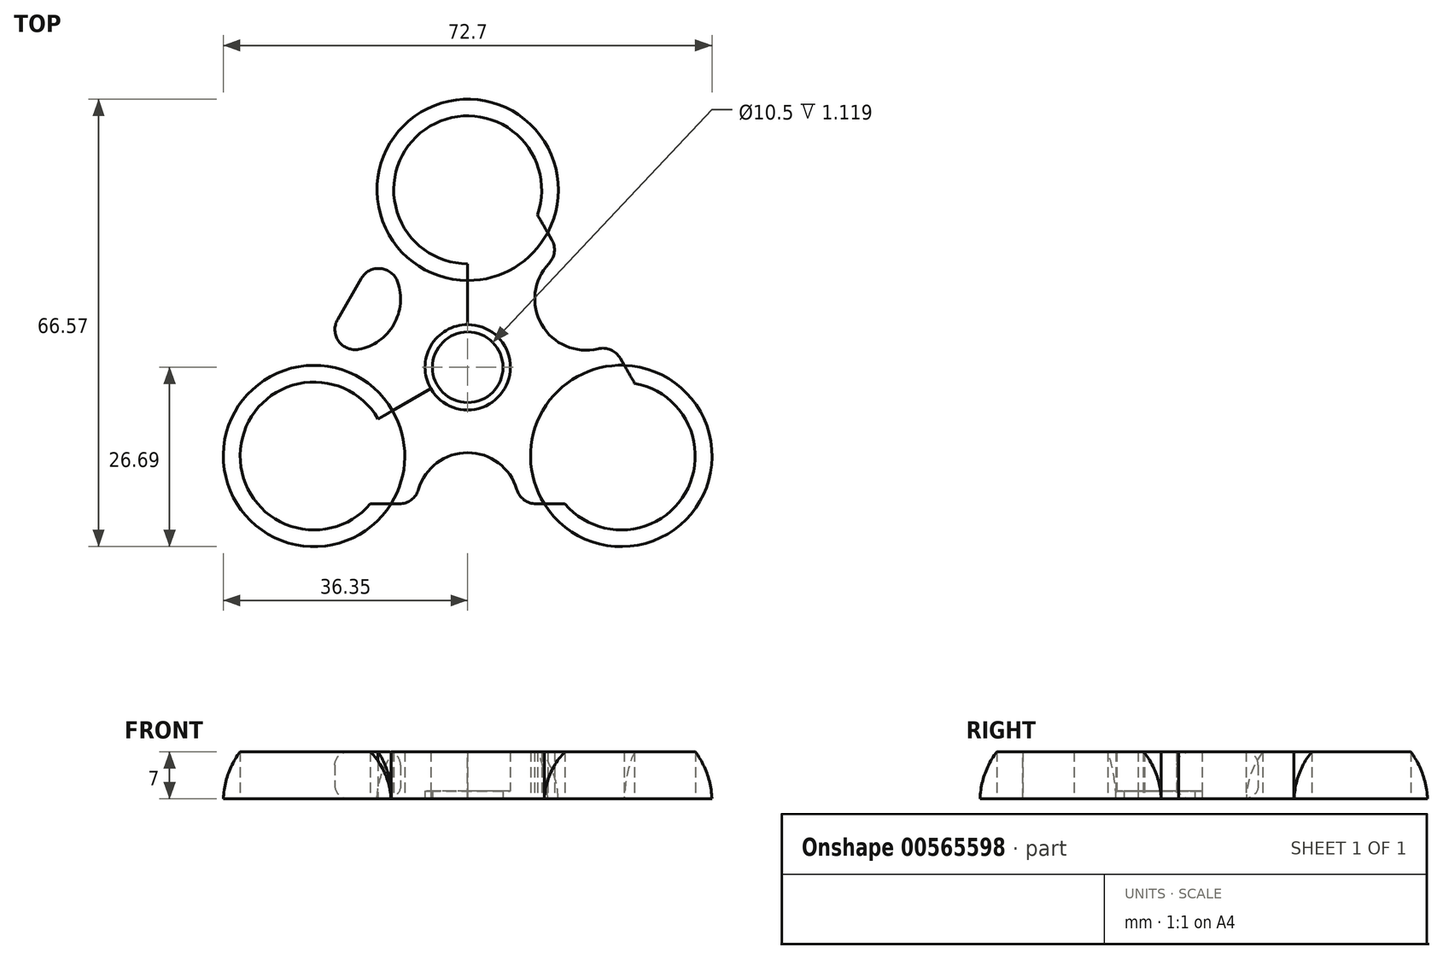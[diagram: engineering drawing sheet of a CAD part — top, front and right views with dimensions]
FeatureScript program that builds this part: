
annotation { "Feature Type Name" : "Feature", "Feature Type Description" : "" }
export const myFeature = defineFeature(function(context is Context, id is Id, definition is map)
    precondition{}
    {
        {
            var Q0;
            Q0=qCreatedBy(makeId("Top.planeOp"),FACE);
            var sketch = newSketch(context, id + "F0", { "sketchPlane" : qUnion([Q0])});
            skCircle(sketch, "E0", {"center": v(0, 0) * mm, "radius": 6.35 * mm});
            skLineSegment(sketch, "E1", {"start": v(0, 0) * mm, "end": v(0, 26.4) * mm});
            skLineSegment(sketch, "E2", {"start": v(0, 0) * mm, "end": v(22.86, -13.2) * mm});
            skLineSegment(sketch, "E3", {"start": v(0, 0) * mm, "end": v(-22.86, -13.2) * mm});
            skCircle(sketch, "E4", {"center": v(-22.86, -13.2) * mm, "radius": 11 * mm});
            skCircle(sketch, "E5", {"center": v(22.86, -13.2) * mm, "radius": 11 * mm});
            skCircle(sketch, "E6", {"center": v(0, 26.4) * mm, "radius": 11 * mm});
            skLineSegment(sketch, "E7", {"start": v(0, 0) * mm, "end": v(-35.2, -20.32) * mm});
            skLineSegment(sketch, "E8", {"start": v(0, 0) * mm, "end": v(35.2, -20.32) * mm});
            skLineSegment(sketch, "E9", {"start": v(0, 0) * mm, "end": v(0, 40.64) * mm});
            skLineSegment(sketch, "E10", {"start": v(-35.2, -20.32) * mm, "end": v(35.2, -20.32) * mm});
            skLineSegment(sketch, "E11", {"start": v(0, 40.64) * mm, "end": v(35.2, -20.32) * mm});
            skLineSegment(sketch, "E12", {"start": v(0, 40.64) * mm, "end": v(-35.2, -20.32) * mm});
            skCircle(sketch, "E13", {"center": v(-22.86, -13.2) * mm, "radius": 13.5 * mm});
            skCircle(sketch, "E14", {"center": v(22.86, -13.2) * mm, "radius": 13.5 * mm});
            skCircle(sketch, "E15", {"center": v(0, 26.4) * mm, "radius": 13.5 * mm});
            skArc(sketch, "E16", {"start": v(-13.79, 16.76) * mm, "mid": v(-11, 6.35) * mm, "end": v(-21.4, 3.56) * mm});
            skArc(sketch, "E17", {"start": v(13.79, 16.76) * mm, "mid": v(11, 6.35) * mm, "end": v(21.4, 3.56) * mm});
            skArc(sketch, "E18", {"start": v(7.62, -20.32) * mm, "mid": v(0, -12.7) * mm, "end": v(-7.62, -20.32) * mm});
            skCircle(sketch, "E19", {"center": v(0, 0) * mm, "radius": 5.25 * mm});
            skSolve(sketch);
        }
        {
            var Q0;
            {var subQ0=sQuery(id+"F0.wireOp",EDGE,"E10");var subQ1=sQuery(id+"F0.wireOp",EDGE,"E5");var subQ2=makeQuery(id+"F0.imprint","INTERSECT",VERTEX,{"disambiguationData":[OD(0.0)],"derivedFrom":[subQ1,subQ0]});Q0=makeQuery(id+"F0.imprint","IMPRINT",FACE,{"disambiguationData":[TD([[makeQuery(id+"F0.imprint","IMPRINT",EDGE,{"disambiguationData":[TD([[subQ2,-1.0]])],"derivedFrom":subQ1}),-1.0]])]});}
            var Q1;
            {var subQ0=sQuery(id+"F0.wireOp",EDGE,"E8");var subQ1=sQuery(id+"F0.wireOp",EDGE,"E5");var subQ2=makeQuery(id+"F0.imprint","INTERSECT",VERTEX,{"disambiguationData":[OD(1.0)],"derivedFrom":[subQ1,subQ0]});Q1=makeQuery(id+"F0.imprint","IMPRINT",FACE,{"disambiguationData":[TD([[makeQuery(id+"F0.imprint","IMPRINT",EDGE,{"disambiguationData":[TD([[subQ2,-1.0]])],"derivedFrom":subQ1}),-1.0]])]});}
            var Q2;
            {var subQ0=sQuery(id+"F0.wireOp",EDGE,"E10");var subQ1=sQuery(id+"F0.wireOp",EDGE,"E5");var subQ2=makeQuery(id+"F0.imprint","INTERSECT",VERTEX,{"disambiguationData":[OD(1.0)],"derivedFrom":[subQ1,subQ0]});Q2=makeQuery(id+"F0.imprint","IMPRINT",FACE,{"disambiguationData":[TD([[makeQuery(id+"F0.imprint","IMPRINT",EDGE,{"disambiguationData":[TD([[subQ2,-1.0]])],"derivedFrom":subQ1}),-1.0]])]});}
            var Q3;
            {var subQ0=sQuery(id+"F0.wireOp",EDGE,"E11");var subQ1=sQuery(id+"F0.wireOp",EDGE,"E5");var subQ2=makeQuery(id+"F0.imprint","INTERSECT",VERTEX,{"disambiguationData":[OD(0.0)],"derivedFrom":[subQ1,subQ0]});Q3=makeQuery(id+"F0.imprint","IMPRINT",FACE,{"disambiguationData":[TD([[makeQuery(id+"F0.imprint","IMPRINT",EDGE,{"disambiguationData":[TD([[subQ2,1.0]])],"derivedFrom":subQ1}),-1.0]])]});}
            var Q4;
            {var subQ0=sQuery(id+"F0.wireOp",EDGE,"E8");var subQ1=sQuery(id+"F0.wireOp",EDGE,"E5");var subQ2=makeQuery(id+"F0.imprint","INTERSECT",VERTEX,{"disambiguationData":[OD(0.0)],"derivedFrom":[subQ1,subQ0]});Q4=makeQuery(id+"F0.imprint","IMPRINT",FACE,{"disambiguationData":[TD([[makeQuery(id+"F0.imprint","IMPRINT",EDGE,{"disambiguationData":[TD([[subQ2,1.0]])],"derivedFrom":subQ1}),-1.0]])]});}
            var Q5;
            {var subQ0=sQuery(id+"F0.wireOp",EDGE,"E8");var subQ1=sQuery(id+"F0.wireOp",EDGE,"E5");var subQ2=makeQuery(id+"F0.imprint","INTERSECT",VERTEX,{"disambiguationData":[OD(0.0)],"derivedFrom":[subQ1,subQ0]});Q5=makeQuery(id+"F0.imprint","IMPRINT",FACE,{"disambiguationData":[TD([[makeQuery(id+"F0.imprint","IMPRINT",EDGE,{"disambiguationData":[TD([[subQ2,-1.0]])],"derivedFrom":subQ1}),-1.0]])]});}
            var Q6;
            {var subQ5=sQuery(id+"F0.wireOp",EDGE,"E18");Q6=makeQuery(id+"F0.imprint","IMPRINT",FACE,{"disambiguationData":[TD([[makeQuery(id+"F0.imprint","IMPRINT",EDGE,{"derivedFrom":subQ5}),-1.0]])]});}
            var Q7;
            {var subQ11=sQuery(id+"F0.wireOp",EDGE,"E17");Q7=makeQuery(id+"F0.imprint","IMPRINT",FACE,{"disambiguationData":[TD([[makeQuery(id+"F0.imprint","IMPRINT",EDGE,{"derivedFrom":subQ11}),-1.0]])]});}
            var Q8;
            {var subQ0=sQuery(id+"F0.wireOp",EDGE,"E16");Q8=makeQuery(id+"F0.imprint","IMPRINT",FACE,{"disambiguationData":[TD([[makeQuery(id+"F0.imprint","IMPRINT",EDGE,{"derivedFrom":subQ0}),1.0]])]});}
            var Q9;
            {var subQ0=sQuery(id+"F0.wireOp",EDGE,"E12");var subQ1=sQuery(id+"F0.wireOp",EDGE,"E4");var subQ2=makeQuery(id+"F0.imprint","INTERSECT",VERTEX,{"disambiguationData":[OD(0.0)],"derivedFrom":[subQ1,subQ0]});Q9=makeQuery(id+"F0.imprint","IMPRINT",FACE,{"disambiguationData":[TD([[makeQuery(id+"F0.imprint","IMPRINT",EDGE,{"disambiguationData":[TD([[subQ2,1.0]])],"derivedFrom":subQ1}),-1.0]])]});}
            var Q10;
            {var subQ0=sQuery(id+"F0.wireOp",EDGE,"E7");var subQ1=sQuery(id+"F0.wireOp",EDGE,"E4");var subQ2=makeQuery(id+"F0.imprint","INTERSECT",VERTEX,{"disambiguationData":[OD(0.0)],"derivedFrom":[subQ1,subQ0]});Q10=makeQuery(id+"F0.imprint","IMPRINT",FACE,{"disambiguationData":[TD([[makeQuery(id+"F0.imprint","IMPRINT",EDGE,{"disambiguationData":[TD([[subQ2,1.0]])],"derivedFrom":subQ1}),-1.0]])]});}
            var Q11;
            {var subQ0=sQuery(id+"F0.wireOp",EDGE,"E10");var subQ1=sQuery(id+"F0.wireOp",EDGE,"E4");var subQ2=makeQuery(id+"F0.imprint","INTERSECT",VERTEX,{"disambiguationData":[OD(0.0)],"derivedFrom":[subQ1,subQ0]});Q11=makeQuery(id+"F0.imprint","IMPRINT",FACE,{"disambiguationData":[TD([[makeQuery(id+"F0.imprint","IMPRINT",EDGE,{"disambiguationData":[TD([[subQ2,-1.0]])],"derivedFrom":subQ1}),-1.0]])]});}
            var Q12;
            {var subQ0=sQuery(id+"F0.wireOp",EDGE,"E12");var subQ1=sQuery(id+"F0.wireOp",EDGE,"E4");var subQ2=makeQuery(id+"F0.imprint","INTERSECT",VERTEX,{"disambiguationData":[OD(1.0)],"derivedFrom":[subQ1,subQ0]});Q12=makeQuery(id+"F0.imprint","IMPRINT",FACE,{"disambiguationData":[TD([[makeQuery(id+"F0.imprint","IMPRINT",EDGE,{"disambiguationData":[TD([[subQ2,-1.0]])],"derivedFrom":subQ1}),-1.0]])]});}
            var Q13;
            {var subQ0=sQuery(id+"F0.wireOp",EDGE,"E7");var subQ1=sQuery(id+"F0.wireOp",EDGE,"E4");var subQ2=makeQuery(id+"F0.imprint","INTERSECT",VERTEX,{"disambiguationData":[OD(1.0)],"derivedFrom":[subQ1,subQ0]});Q13=makeQuery(id+"F0.imprint","IMPRINT",FACE,{"disambiguationData":[TD([[makeQuery(id+"F0.imprint","IMPRINT",EDGE,{"disambiguationData":[TD([[subQ2,-1.0]])],"derivedFrom":subQ1}),-1.0]])]});}
            var Q14;
            {var subQ0=sQuery(id+"F0.wireOp",EDGE,"E12");var subQ1=sQuery(id+"F0.wireOp",EDGE,"E4");var subQ2=makeQuery(id+"F0.imprint","INTERSECT",VERTEX,{"disambiguationData":[OD(0.0)],"derivedFrom":[subQ1,subQ0]});Q14=makeQuery(id+"F0.imprint","IMPRINT",FACE,{"disambiguationData":[TD([[makeQuery(id+"F0.imprint","IMPRINT",EDGE,{"disambiguationData":[TD([[subQ2,-1.0]])],"derivedFrom":subQ1}),-1.0]])]});}
            var Q15;
            {var subQ0=sQuery(id+"F0.wireOp",EDGE,"E9");var subQ1=sQuery(id+"F0.wireOp",EDGE,"E6");var subQ2=makeQuery(id+"F0.imprint","INTERSECT",VERTEX,{"disambiguationData":[OD(1.0)],"derivedFrom":[subQ1,subQ0]});Q15=makeQuery(id+"F0.imprint","IMPRINT",FACE,{"disambiguationData":[TD([[makeQuery(id+"F0.imprint","IMPRINT",EDGE,{"disambiguationData":[TD([[subQ2,-1.0]])],"derivedFrom":subQ1}),-1.0]])]});}
            var Q16;
            {var subQ0=sQuery(id+"F0.wireOp",EDGE,"E12");var subQ1=sQuery(id+"F0.wireOp",EDGE,"E6");var subQ2=makeQuery(id+"F0.imprint","INTERSECT",VERTEX,{"disambiguationData":[OD(1.0)],"derivedFrom":[subQ1,subQ0]});Q16=makeQuery(id+"F0.imprint","IMPRINT",FACE,{"disambiguationData":[TD([[makeQuery(id+"F0.imprint","IMPRINT",EDGE,{"disambiguationData":[TD([[subQ2,-1.0]])],"derivedFrom":subQ1}),-1.0]])]});}
            var Q17;
            {var subQ0=sQuery(id+"F0.wireOp",EDGE,"E12");var subQ1=sQuery(id+"F0.wireOp",EDGE,"E6");var subQ2=makeQuery(id+"F0.imprint","INTERSECT",VERTEX,{"disambiguationData":[OD(0.0)],"derivedFrom":[subQ1,subQ0]});Q17=makeQuery(id+"F0.imprint","IMPRINT",FACE,{"disambiguationData":[TD([[makeQuery(id+"F0.imprint","IMPRINT",EDGE,{"disambiguationData":[TD([[subQ2,-1.0]])],"derivedFrom":subQ1}),-1.0]])]});}
            var Q18;
            {var subQ0=sQuery(id+"F0.wireOp",EDGE,"E11");var subQ1=sQuery(id+"F0.wireOp",EDGE,"E6");var subQ2=makeQuery(id+"F0.imprint","INTERSECT",VERTEX,{"disambiguationData":[OD(0.0)],"derivedFrom":[subQ1,subQ0]});Q18=makeQuery(id+"F0.imprint","IMPRINT",FACE,{"disambiguationData":[TD([[makeQuery(id+"F0.imprint","IMPRINT",EDGE,{"disambiguationData":[TD([[subQ2,1.0]])],"derivedFrom":subQ1}),-1.0]])]});}
            var Q19;
            {var subQ0=sQuery(id+"F0.wireOp",EDGE,"E9");var subQ1=sQuery(id+"F0.wireOp",EDGE,"E6");var subQ2=makeQuery(id+"F0.imprint","INTERSECT",VERTEX,{"disambiguationData":[OD(0.0)],"derivedFrom":[subQ1,subQ0]});Q19=makeQuery(id+"F0.imprint","IMPRINT",FACE,{"disambiguationData":[TD([[makeQuery(id+"F0.imprint","IMPRINT",EDGE,{"disambiguationData":[TD([[subQ2,1.0]])],"derivedFrom":subQ1}),-1.0]])]});}
            var Q20;
            {var subQ0=sQuery(id+"F0.wireOp",EDGE,"E9");var subQ1=sQuery(id+"F0.wireOp",EDGE,"E6");var subQ2=makeQuery(id+"F0.imprint","INTERSECT",VERTEX,{"disambiguationData":[OD(0.0)],"derivedFrom":[subQ1,subQ0]});Q20=makeQuery(id+"F0.imprint","IMPRINT",FACE,{"disambiguationData":[TD([[makeQuery(id+"F0.imprint","IMPRINT",EDGE,{"disambiguationData":[TD([[subQ2,-1.0]])],"derivedFrom":subQ1}),-1.0]])]});}
            extrude(context, id + "F1", {"entities" : qUnion([Q0, Q1, Q2, Q3, Q4, Q5, Q6, Q7, Q8, Q9, Q10, Q11, Q12, Q13, Q14, Q15, Q16, Q17, Q18, Q19, Q20]), "depth" : 7 * mm, "offsetDistance" : 25.4 * mm});
        }
        {
            var Q0;
            {var subQ0=sQuery(id+"F0.wireOp",EDGE,"E18");var subQ1=sQuery(id+"F0.wireOp",EDGE,"E10");Q0=makeQuery(id+"F1.opExtrude","SWEPT_EDGE",EDGE,{"disambiguationData":[OSD([subQ1,subQ0]),TDD([makeQuery(id+"F0.imprint","INTERSECT",VERTEX,{"disambiguationData":[OD(1.0)],"derivedFrom":[subQ1,subQ0]})])]});}
            var Q1;
            {var subQ0=sQuery(id+"F0.wireOp",EDGE,"E18");var subQ1=sQuery(id+"F0.wireOp",EDGE,"E10");Q1=makeQuery(id+"F1.opExtrude","SWEPT_EDGE",EDGE,{"disambiguationData":[OSD([subQ1,subQ0]),TDD([makeQuery(id+"F0.imprint","INTERSECT",VERTEX,{"disambiguationData":[OD(0.0)],"derivedFrom":[subQ1,subQ0]})])]});}
            var Q2;
            {var subQ0=sQuery(id+"F0.wireOp",EDGE,"E16");var subQ1=sQuery(id+"F0.wireOp",EDGE,"E12");Q2=makeQuery(id+"F1.opExtrude","SWEPT_EDGE",EDGE,{"disambiguationData":[OSD([subQ1,subQ0]),TDD([makeQuery(id+"F0.imprint","INTERSECT",VERTEX,{"disambiguationData":[OD(0.0)],"derivedFrom":[subQ1,subQ0]})])]});}
            var Q3;
            {var subQ0=sQuery(id+"F0.wireOp",EDGE,"E16");var subQ1=sQuery(id+"F0.wireOp",EDGE,"E12");Q3=makeQuery(id+"F1.opExtrude","SWEPT_EDGE",EDGE,{"disambiguationData":[OSD([subQ1,subQ0]),TDD([makeQuery(id+"F0.imprint","INTERSECT",VERTEX,{"disambiguationData":[OD(1.0)],"derivedFrom":[subQ1,subQ0]})])]});}
            var Q4;
            {var subQ0=sQuery(id+"F0.wireOp",EDGE,"E17");var subQ1=sQuery(id+"F0.wireOp",EDGE,"E11");Q4=makeQuery(id+"F1.opExtrude","SWEPT_EDGE",EDGE,{"disambiguationData":[OSD([subQ1,subQ0]),TDD([makeQuery(id+"F0.imprint","INTERSECT",VERTEX,{"disambiguationData":[OD(1.0)],"derivedFrom":[subQ1,subQ0]})])]});}
            var Q5;
            {var subQ0=sQuery(id+"F0.wireOp",EDGE,"E17");var subQ1=sQuery(id+"F0.wireOp",EDGE,"E11");Q5=makeQuery(id+"F1.opExtrude","SWEPT_EDGE",EDGE,{"disambiguationData":[OSD([subQ1,subQ0]),TDD([makeQuery(id+"F0.imprint","INTERSECT",VERTEX,{"disambiguationData":[OD(0.0)],"derivedFrom":[subQ1,subQ0]})])]});}
            fillet(context, id + "F2", {"entities" : qUnion([Q0, Q1, Q2, Q3, Q4, Q5]), "radius" : 3 * mm, "tangentPropagation" : true, "allowEdgeOverflow" : false});
        }
        {
            var Q0;
            Q0=makeQuery(id+"F1.opExtrude","CAP_EDGE",EDGE,{"disambiguationData":[OSD([sQuery(id+"F0.wireOp",EDGE,"E15")])],"isStart":false});
            var Q1;
            {var subQ0=sQuery(id+"F0.wireOp",EDGE,"E11");Q1=makeQuery(id+"F1.opExtrude","CAP_EDGE",EDGE,{"disambiguationData":[OSD([subQ0]),TDD([makeQuery(id+"F0.imprint","IMPRINT",EDGE,{"disambiguationData":[TD([[makeQuery(id+"F0.imprint","INTERSECT",VERTEX,{"disambiguationData":[OD(0.0)],"derivedFrom":[subQ0,sQuery(id+"F0.wireOp",EDGE,"E17")]}),1.0]])],"derivedFrom":subQ0})])],"isStart":false});}
            var Q2;
            {var subQ0=sQuery(id+"F0.wireOp",EDGE,"E17");var subQ1=sQuery(id+"F0.wireOp",EDGE,"E11");Q2=makeQuery(id+"F2.opFillet","BLEND_EDGE",EDGE,{"blendedFrom":[makeQuery(id+"F1.opExtrude","SWEPT_EDGE",EDGE,{"disambiguationData":[OSD([subQ1,subQ0]),TDD([makeQuery(id+"F0.imprint","INTERSECT",VERTEX,{"disambiguationData":[OD(0.0)],"derivedFrom":[subQ1,subQ0]})])]}),makeQuery(id+"F1.opExtrude","CAP_FACE",FACE,{"disambiguationData":[OSD([sQuery(id+"F0.wireOp",EDGE,"E0"),sQuery(id+"F0.wireOp",EDGE,"E4"),sQuery(id+"F0.wireOp",EDGE,"E5"),sQuery(id+"F0.wireOp",EDGE,"E6"),sQuery(id+"F0.wireOp",EDGE,"E10"),subQ1,sQuery(id+"F0.wireOp",EDGE,"E12"),sQuery(id+"F0.wireOp",EDGE,"E13"),sQuery(id+"F0.wireOp",EDGE,"E14"),sQuery(id+"F0.wireOp",EDGE,"E15"),sQuery(id+"F0.wireOp",EDGE,"E16"),subQ0,sQuery(id+"F0.wireOp",EDGE,"E18")])],"isStart":false})],"blendedInto":[makeQuery(id+"F1.opExtrude","CAP_FACE",FACE,{"disambiguationData":[OSD([sQuery(id+"F0.wireOp",EDGE,"E0"),sQuery(id+"F0.wireOp",EDGE,"E4"),sQuery(id+"F0.wireOp",EDGE,"E5"),sQuery(id+"F0.wireOp",EDGE,"E6"),sQuery(id+"F0.wireOp",EDGE,"E10"),subQ1,sQuery(id+"F0.wireOp",EDGE,"E12"),sQuery(id+"F0.wireOp",EDGE,"E13"),sQuery(id+"F0.wireOp",EDGE,"E14"),sQuery(id+"F0.wireOp",EDGE,"E15"),sQuery(id+"F0.wireOp",EDGE,"E16"),subQ0,sQuery(id+"F0.wireOp",EDGE,"E18")])],"isStart":false})]});}
            var Q3;
            Q3=makeQuery(id+"F1.opExtrude","CAP_EDGE",EDGE,{"disambiguationData":[OSD([sQuery(id+"F0.wireOp",EDGE,"E17")])],"isStart":false});
            var Q4;
            {var subQ0=sQuery(id+"F0.wireOp",EDGE,"E17");var subQ1=sQuery(id+"F0.wireOp",EDGE,"E11");Q4=makeQuery(id+"F2.opFillet","BLEND_EDGE",EDGE,{"blendedFrom":[makeQuery(id+"F1.opExtrude","SWEPT_EDGE",EDGE,{"disambiguationData":[OSD([subQ1,subQ0]),TDD([makeQuery(id+"F0.imprint","INTERSECT",VERTEX,{"disambiguationData":[OD(1.0)],"derivedFrom":[subQ1,subQ0]})])]}),makeQuery(id+"F1.opExtrude","CAP_FACE",FACE,{"disambiguationData":[OSD([sQuery(id+"F0.wireOp",EDGE,"E0"),sQuery(id+"F0.wireOp",EDGE,"E4"),sQuery(id+"F0.wireOp",EDGE,"E5"),sQuery(id+"F0.wireOp",EDGE,"E6"),sQuery(id+"F0.wireOp",EDGE,"E10"),subQ1,sQuery(id+"F0.wireOp",EDGE,"E12"),sQuery(id+"F0.wireOp",EDGE,"E13"),sQuery(id+"F0.wireOp",EDGE,"E14"),sQuery(id+"F0.wireOp",EDGE,"E15"),sQuery(id+"F0.wireOp",EDGE,"E16"),subQ0,sQuery(id+"F0.wireOp",EDGE,"E18")])],"isStart":false})],"blendedInto":[makeQuery(id+"F1.opExtrude","CAP_FACE",FACE,{"disambiguationData":[OSD([sQuery(id+"F0.wireOp",EDGE,"E0"),sQuery(id+"F0.wireOp",EDGE,"E4"),sQuery(id+"F0.wireOp",EDGE,"E5"),sQuery(id+"F0.wireOp",EDGE,"E6"),sQuery(id+"F0.wireOp",EDGE,"E10"),subQ1,sQuery(id+"F0.wireOp",EDGE,"E12"),sQuery(id+"F0.wireOp",EDGE,"E13"),sQuery(id+"F0.wireOp",EDGE,"E14"),sQuery(id+"F0.wireOp",EDGE,"E15"),sQuery(id+"F0.wireOp",EDGE,"E16"),subQ0,sQuery(id+"F0.wireOp",EDGE,"E18")])],"isStart":false})]});}
            var Q5;
            {var subQ0=sQuery(id+"F0.wireOp",EDGE,"E11");Q5=makeQuery(id+"F1.opExtrude","CAP_EDGE",EDGE,{"disambiguationData":[OSD([subQ0]),TDD([makeQuery(id+"F0.imprint","IMPRINT",EDGE,{"disambiguationData":[TD([[makeQuery(id+"F0.imprint","INTERSECT",VERTEX,{"disambiguationData":[OD(1.0)],"derivedFrom":[subQ0,sQuery(id+"F0.wireOp",EDGE,"E17")]}),-1.0]])],"derivedFrom":subQ0})])],"isStart":false});}
            var Q6;
            Q6=makeQuery(id+"F1.opExtrude","CAP_EDGE",EDGE,{"disambiguationData":[OSD([sQuery(id+"F0.wireOp",EDGE,"E14")])],"isStart":false});
            var Q7;
            {var subQ0=sQuery(id+"F0.wireOp",EDGE,"E10");Q7=makeQuery(id+"F1.opExtrude","CAP_EDGE",EDGE,{"disambiguationData":[OSD([subQ0]),TDD([makeQuery(id+"F0.imprint","IMPRINT",EDGE,{"disambiguationData":[TD([[makeQuery(id+"F0.imprint","INTERSECT",VERTEX,{"disambiguationData":[OD(0.0)],"derivedFrom":[subQ0,sQuery(id+"F0.wireOp",EDGE,"E18")]}),-1.0]])],"derivedFrom":subQ0})])],"isStart":false});}
            var Q8;
            {var subQ0=sQuery(id+"F0.wireOp",EDGE,"E18");var subQ1=sQuery(id+"F0.wireOp",EDGE,"E10");Q8=makeQuery(id+"F2.opFillet","BLEND_EDGE",EDGE,{"blendedFrom":[makeQuery(id+"F1.opExtrude","SWEPT_EDGE",EDGE,{"disambiguationData":[OSD([subQ1,subQ0]),TDD([makeQuery(id+"F0.imprint","INTERSECT",VERTEX,{"disambiguationData":[OD(0.0)],"derivedFrom":[subQ1,subQ0]})])]}),makeQuery(id+"F1.opExtrude","CAP_FACE",FACE,{"disambiguationData":[OSD([sQuery(id+"F0.wireOp",EDGE,"E0"),sQuery(id+"F0.wireOp",EDGE,"E4"),sQuery(id+"F0.wireOp",EDGE,"E5"),sQuery(id+"F0.wireOp",EDGE,"E6"),subQ1,sQuery(id+"F0.wireOp",EDGE,"E11"),sQuery(id+"F0.wireOp",EDGE,"E12"),sQuery(id+"F0.wireOp",EDGE,"E13"),sQuery(id+"F0.wireOp",EDGE,"E14"),sQuery(id+"F0.wireOp",EDGE,"E15"),sQuery(id+"F0.wireOp",EDGE,"E16"),sQuery(id+"F0.wireOp",EDGE,"E17"),subQ0])],"isStart":false})],"blendedInto":[makeQuery(id+"F1.opExtrude","CAP_FACE",FACE,{"disambiguationData":[OSD([sQuery(id+"F0.wireOp",EDGE,"E0"),sQuery(id+"F0.wireOp",EDGE,"E4"),sQuery(id+"F0.wireOp",EDGE,"E5"),sQuery(id+"F0.wireOp",EDGE,"E6"),subQ1,sQuery(id+"F0.wireOp",EDGE,"E11"),sQuery(id+"F0.wireOp",EDGE,"E12"),sQuery(id+"F0.wireOp",EDGE,"E13"),sQuery(id+"F0.wireOp",EDGE,"E14"),sQuery(id+"F0.wireOp",EDGE,"E15"),sQuery(id+"F0.wireOp",EDGE,"E16"),sQuery(id+"F0.wireOp",EDGE,"E17"),subQ0])],"isStart":false})]});}
            var Q9;
            Q9=makeQuery(id+"F1.opExtrude","CAP_EDGE",EDGE,{"disambiguationData":[OSD([sQuery(id+"F0.wireOp",EDGE,"E18")])],"isStart":false});
            var Q10;
            {var subQ0=sQuery(id+"F0.wireOp",EDGE,"E18");var subQ1=sQuery(id+"F0.wireOp",EDGE,"E10");Q10=makeQuery(id+"F2.opFillet","BLEND_EDGE",EDGE,{"blendedFrom":[makeQuery(id+"F1.opExtrude","SWEPT_EDGE",EDGE,{"disambiguationData":[OSD([subQ1,subQ0]),TDD([makeQuery(id+"F0.imprint","INTERSECT",VERTEX,{"disambiguationData":[OD(1.0)],"derivedFrom":[subQ1,subQ0]})])]}),makeQuery(id+"F1.opExtrude","CAP_FACE",FACE,{"disambiguationData":[OSD([sQuery(id+"F0.wireOp",EDGE,"E0"),sQuery(id+"F0.wireOp",EDGE,"E4"),sQuery(id+"F0.wireOp",EDGE,"E5"),sQuery(id+"F0.wireOp",EDGE,"E6"),subQ1,sQuery(id+"F0.wireOp",EDGE,"E11"),sQuery(id+"F0.wireOp",EDGE,"E12"),sQuery(id+"F0.wireOp",EDGE,"E13"),sQuery(id+"F0.wireOp",EDGE,"E14"),sQuery(id+"F0.wireOp",EDGE,"E15"),sQuery(id+"F0.wireOp",EDGE,"E16"),sQuery(id+"F0.wireOp",EDGE,"E17"),subQ0])],"isStart":false})],"blendedInto":[makeQuery(id+"F1.opExtrude","CAP_FACE",FACE,{"disambiguationData":[OSD([sQuery(id+"F0.wireOp",EDGE,"E0"),sQuery(id+"F0.wireOp",EDGE,"E4"),sQuery(id+"F0.wireOp",EDGE,"E5"),sQuery(id+"F0.wireOp",EDGE,"E6"),subQ1,sQuery(id+"F0.wireOp",EDGE,"E11"),sQuery(id+"F0.wireOp",EDGE,"E12"),sQuery(id+"F0.wireOp",EDGE,"E13"),sQuery(id+"F0.wireOp",EDGE,"E14"),sQuery(id+"F0.wireOp",EDGE,"E15"),sQuery(id+"F0.wireOp",EDGE,"E16"),sQuery(id+"F0.wireOp",EDGE,"E17"),subQ0])],"isStart":false})]});}
            var Q11;
            {var subQ0=sQuery(id+"F0.wireOp",EDGE,"E10");Q11=makeQuery(id+"F1.opExtrude","CAP_EDGE",EDGE,{"disambiguationData":[OSD([subQ0]),TDD([makeQuery(id+"F0.imprint","IMPRINT",EDGE,{"disambiguationData":[TD([[makeQuery(id+"F0.imprint","INTERSECT",VERTEX,{"disambiguationData":[OD(1.0)],"derivedFrom":[subQ0,sQuery(id+"F0.wireOp",EDGE,"E18")]}),1.0]])],"derivedFrom":subQ0})])],"isStart":false});}
            var Q12;
            Q12=makeQuery(id+"F1.opExtrude","CAP_EDGE",EDGE,{"disambiguationData":[OSD([sQuery(id+"F0.wireOp",EDGE,"E13")])],"isStart":false});
            var Q13;
            {var subQ0=sQuery(id+"F0.wireOp",EDGE,"E12");Q13=makeQuery(id+"F1.opExtrude","CAP_EDGE",EDGE,{"disambiguationData":[OSD([subQ0]),TDD([makeQuery(id+"F0.imprint","IMPRINT",EDGE,{"disambiguationData":[TD([[makeQuery(id+"F0.imprint","INTERSECT",VERTEX,{"disambiguationData":[OD(1.0)],"derivedFrom":[subQ0,sQuery(id+"F0.wireOp",EDGE,"E16")]}),-1.0]])],"derivedFrom":subQ0})])],"isStart":false});}
            var Q14;
            {var subQ0=sQuery(id+"F0.wireOp",EDGE,"E16");var subQ1=sQuery(id+"F0.wireOp",EDGE,"E12");Q14=makeQuery(id+"F2.opFillet","BLEND_EDGE",EDGE,{"blendedFrom":[makeQuery(id+"F1.opExtrude","SWEPT_EDGE",EDGE,{"disambiguationData":[OSD([subQ1,subQ0]),TDD([makeQuery(id+"F0.imprint","INTERSECT",VERTEX,{"disambiguationData":[OD(1.0)],"derivedFrom":[subQ1,subQ0]})])]}),makeQuery(id+"F1.opExtrude","CAP_FACE",FACE,{"disambiguationData":[OSD([sQuery(id+"F0.wireOp",EDGE,"E0"),sQuery(id+"F0.wireOp",EDGE,"E4"),sQuery(id+"F0.wireOp",EDGE,"E5"),sQuery(id+"F0.wireOp",EDGE,"E6"),sQuery(id+"F0.wireOp",EDGE,"E10"),sQuery(id+"F0.wireOp",EDGE,"E11"),subQ1,sQuery(id+"F0.wireOp",EDGE,"E13"),sQuery(id+"F0.wireOp",EDGE,"E14"),sQuery(id+"F0.wireOp",EDGE,"E15"),subQ0,sQuery(id+"F0.wireOp",EDGE,"E17"),sQuery(id+"F0.wireOp",EDGE,"E18")])],"isStart":false})],"blendedInto":[makeQuery(id+"F1.opExtrude","CAP_FACE",FACE,{"disambiguationData":[OSD([sQuery(id+"F0.wireOp",EDGE,"E0"),sQuery(id+"F0.wireOp",EDGE,"E4"),sQuery(id+"F0.wireOp",EDGE,"E5"),sQuery(id+"F0.wireOp",EDGE,"E6"),sQuery(id+"F0.wireOp",EDGE,"E10"),sQuery(id+"F0.wireOp",EDGE,"E11"),subQ1,sQuery(id+"F0.wireOp",EDGE,"E13"),sQuery(id+"F0.wireOp",EDGE,"E14"),sQuery(id+"F0.wireOp",EDGE,"E15"),subQ0,sQuery(id+"F0.wireOp",EDGE,"E17"),sQuery(id+"F0.wireOp",EDGE,"E18")])],"isStart":false})]});}
            var Q15;
            {var subQ0=sQuery(id+"F0.wireOp",EDGE,"E12");Q15=makeQuery(id+"F1.opExtrude","CAP_EDGE",EDGE,{"disambiguationData":[OSD([subQ0]),TDD([makeQuery(id+"F0.imprint","IMPRINT",EDGE,{"disambiguationData":[TD([[makeQuery(id+"F0.imprint","INTERSECT",VERTEX,{"disambiguationData":[OD(0.0)],"derivedFrom":[subQ0,sQuery(id+"F0.wireOp",EDGE,"E16")]}),1.0]])],"derivedFrom":subQ0})])],"isStart":false});}
            var Q16;
            {var subQ0=sQuery(id+"F0.wireOp",EDGE,"E16");var subQ1=sQuery(id+"F0.wireOp",EDGE,"E12");Q16=makeQuery(id+"F2.opFillet","BLEND_EDGE",EDGE,{"blendedFrom":[makeQuery(id+"F1.opExtrude","SWEPT_EDGE",EDGE,{"disambiguationData":[OSD([subQ1,subQ0]),TDD([makeQuery(id+"F0.imprint","INTERSECT",VERTEX,{"disambiguationData":[OD(0.0)],"derivedFrom":[subQ1,subQ0]})])]}),makeQuery(id+"F1.opExtrude","CAP_FACE",FACE,{"disambiguationData":[OSD([sQuery(id+"F0.wireOp",EDGE,"E0"),sQuery(id+"F0.wireOp",EDGE,"E4"),sQuery(id+"F0.wireOp",EDGE,"E5"),sQuery(id+"F0.wireOp",EDGE,"E6"),sQuery(id+"F0.wireOp",EDGE,"E10"),sQuery(id+"F0.wireOp",EDGE,"E11"),subQ1,sQuery(id+"F0.wireOp",EDGE,"E13"),sQuery(id+"F0.wireOp",EDGE,"E14"),sQuery(id+"F0.wireOp",EDGE,"E15"),subQ0,sQuery(id+"F0.wireOp",EDGE,"E17"),sQuery(id+"F0.wireOp",EDGE,"E18")])],"isStart":false})],"blendedInto":[makeQuery(id+"F1.opExtrude","CAP_FACE",FACE,{"disambiguationData":[OSD([sQuery(id+"F0.wireOp",EDGE,"E0"),sQuery(id+"F0.wireOp",EDGE,"E4"),sQuery(id+"F0.wireOp",EDGE,"E5"),sQuery(id+"F0.wireOp",EDGE,"E6"),sQuery(id+"F0.wireOp",EDGE,"E10"),sQuery(id+"F0.wireOp",EDGE,"E11"),subQ1,sQuery(id+"F0.wireOp",EDGE,"E13"),sQuery(id+"F0.wireOp",EDGE,"E14"),sQuery(id+"F0.wireOp",EDGE,"E15"),subQ0,sQuery(id+"F0.wireOp",EDGE,"E17"),sQuery(id+"F0.wireOp",EDGE,"E18")])],"isStart":false})]});}
            var Q17;
            Q17=makeQuery(id+"F1.opExtrude","CAP_EDGE",EDGE,{"disambiguationData":[OSD([sQuery(id+"F0.wireOp",EDGE,"E16")])],"isStart":false});
            fillet(context, id + "F3", {"entities" : qUnion([Q0, Q1, Q2, Q3, Q4, Q5, Q6, Q7, Q8, Q9, Q10, Q11, Q12, Q13, Q14, Q15, Q16, Q17]), "radius" : 12.7 * mm, "tangentPropagation" : true, "allowEdgeOverflow" : false});
        }
        {
            var Q0;
            Q0=makeQuery(id+"F1.opExtrude","CAP_EDGE",EDGE,{"disambiguationData":[OSD([sQuery(id+"F0.wireOp",EDGE,"E16")])],"isStart":false});
            var Q1;
            Q1=makeQuery(id+"F1.opExtrude","CAP_EDGE",EDGE,{"disambiguationData":[OSD([sQuery(id+"F0.wireOp",EDGE,"E15")])],"isStart":false});
            var Q2;
            Q2=makeQuery(id+"F1.opExtrude","CAP_EDGE",EDGE,{"disambiguationData":[OSD([sQuery(id+"F0.wireOp",EDGE,"E17")])],"isStart":false});
            var Q3;
            Q3=makeQuery(id+"F1.opExtrude","CAP_EDGE",EDGE,{"disambiguationData":[OSD([sQuery(id+"F0.wireOp",EDGE,"E18")])],"isStart":false});
            var Q4;
            Q4=makeQuery(id+"F1.opExtrude","CAP_EDGE",EDGE,{"disambiguationData":[OSD([sQuery(id+"F0.wireOp",EDGE,"E13")])],"isStart":false});
            var Q5;
            Q5=makeQuery(id+"F1.opExtrude","CAP_EDGE",EDGE,{"disambiguationData":[OSD([sQuery(id+"F0.wireOp",EDGE,"E14")])],"isStart":false});
            var Q6;
            Q6=makeQuery(id+"F1.opExtrude","CAP_EDGE",EDGE,{"disambiguationData":[OSD([sQuery(id+"F0.wireOp",EDGE,"E17")])],"isStart":true});
            var Q7;
            Q7=makeQuery(id+"F1.opExtrude","CAP_EDGE",EDGE,{"disambiguationData":[OSD([sQuery(id+"F0.wireOp",EDGE,"E15")])],"isStart":true});
            var Q8;
            Q8=makeQuery(id+"F1.opExtrude","CAP_EDGE",EDGE,{"disambiguationData":[OSD([sQuery(id+"F0.wireOp",EDGE,"E16")])],"isStart":true});
            var Q9;
            Q9=makeQuery(id+"F1.opExtrude","CAP_EDGE",EDGE,{"disambiguationData":[OSD([sQuery(id+"F0.wireOp",EDGE,"E18")])],"isStart":true});
            var Q10;
            Q10=makeQuery(id+"F1.opExtrude","CAP_EDGE",EDGE,{"disambiguationData":[OSD([sQuery(id+"F0.wireOp",EDGE,"E14")])],"isStart":true});
            var Q11;
            Q11=makeQuery(id+"F1.opExtrude","CAP_EDGE",EDGE,{"disambiguationData":[OSD([sQuery(id+"F0.wireOp",EDGE,"E13")])],"isStart":true});
            fillet(context, id + "F4", {"entities" : qUnion([Q0, Q1, Q2, Q3, Q4, Q5, Q6, Q7, Q8, Q9, Q10, Q11]), "radius" : 2 * mm, "tangentPropagation" : true, "allowEdgeOverflow" : false});
        }
        {
            var Q0;
            {var subQ0=sQuery(id+"F0.wireOp",EDGE,"E7");var subQ1=sQuery(id+"F0.wireOp",EDGE,"E0");var subQ2=makeQuery(id+"F0.imprint","INTERSECT",VERTEX,{"derivedFrom":[subQ1,subQ0]});Q0=makeQuery(id+"F0.imprint","IMPRINT",FACE,{"disambiguationData":[TD([[makeQuery(id+"F0.imprint","IMPRINT",EDGE,{"disambiguationData":[TD([[subQ2,1.0]])],"derivedFrom":subQ1}),1.0]])]});}
            var Q1;
            {var subQ0=sQuery(id+"F0.wireOp",EDGE,"E9");var subQ1=sQuery(id+"F0.wireOp",EDGE,"E0");var subQ2=makeQuery(id+"F0.imprint","INTERSECT",VERTEX,{"derivedFrom":[subQ1,subQ0]});Q1=makeQuery(id+"F0.imprint","IMPRINT",FACE,{"disambiguationData":[TD([[makeQuery(id+"F0.imprint","IMPRINT",EDGE,{"disambiguationData":[TD([[subQ2,1.0]])],"derivedFrom":subQ1}),1.0]])]});}
            var Q2;
            {var subQ0=sQuery(id+"F0.wireOp",EDGE,"E7");var subQ1=sQuery(id+"F0.wireOp",EDGE,"E0");var subQ2=makeQuery(id+"F0.imprint","INTERSECT",VERTEX,{"derivedFrom":[subQ1,subQ0]});Q2=makeQuery(id+"F0.imprint","IMPRINT",FACE,{"disambiguationData":[TD([[makeQuery(id+"F0.imprint","IMPRINT",EDGE,{"disambiguationData":[TD([[subQ2,-1.0]])],"derivedFrom":subQ1}),1.0]])]});}
            extrude(context, id + "F5", {"entities" : qUnion([Q0, Q1, Q2]), "operationType" : NewBodyOperationType.ADD, "depth" : 1.12 * mm, "offsetDistance" : 25.4 * mm});
        }
    });
